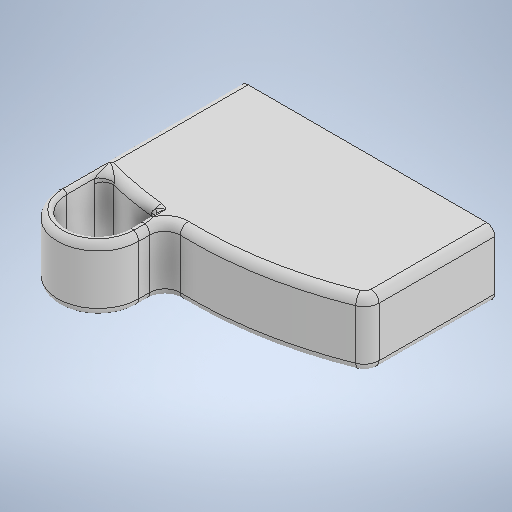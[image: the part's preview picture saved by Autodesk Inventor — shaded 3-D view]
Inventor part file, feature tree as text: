
AUTODESK INVENTOR PART (.ipt)
format: ipt  version: 2025.2 (Build 292293000, 293)  size: 427,520 bytes
history: native  units: in
note: dims shown in document units (in); Inventor stores cm internally (conversion verified against a paired STEP export)
features: fillet x6, other x1, extrude x1, sketch x1
ambient origin geometry x8: Origin, YZ Plane, XZ Plane, XY Plane, X Axis, Y Axis, Z Axis, Center Point
bodies: Body1 (feature_tree)
feature tree (9):
  other  "ソリッド1"
  extrude  "押し出し1"  Depth=3.3465in
  fillet  "フィレット4"  Radius=0.2756in
  fillet  "フィレット8"  Radius=9.8425in
  fillet  "フィレット9"  Radius=0.8661in
  fillet  "フィレット10"  Radius=0.8268in
  fillet  "フィレット11"  Radius=0.1181in
  fillet  "フィレット12"  Radius=0.1181in
  sketch  "スケッチ1"
